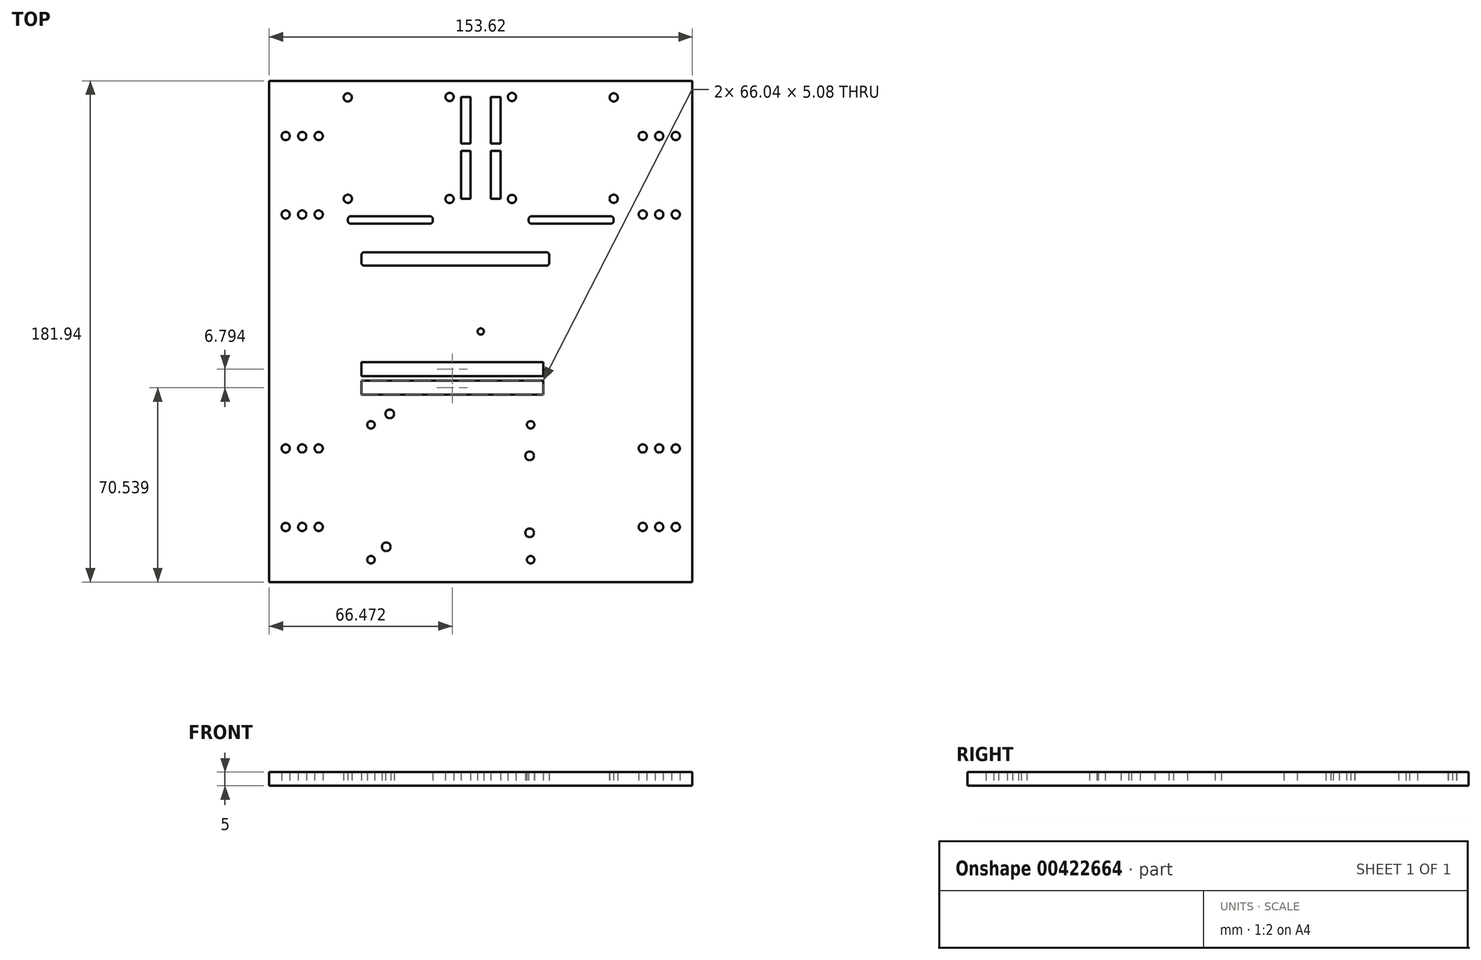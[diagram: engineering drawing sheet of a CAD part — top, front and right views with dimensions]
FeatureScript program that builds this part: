
annotation { "Feature Type Name" : "Feature", "Feature Type Description" : "" }
export const myFeature = defineFeature(function(context is Context, id is Id, definition is map)
    precondition{}
    {
        {
            var Q0;
            Q0=qCreatedBy(makeId("Top.planeOp"),FACE);
            var sketch = newSketch(context, id + "F0", { "sketchPlane" : qUnion([Q0])});
            skLineSegment(sketch, "E0.bottom", {"start": v(-70.46, 90.97) * mm, "end": v(70.46, 90.97) * mm});
            skLineSegment(sketch, "E0.top", {"start": v(-70.46, -90.97) * mm, "end": v(70.46, -90.97) * mm});
            skLineSegment(sketch, "E0.left", {"start": v(-76.8, 84.62) * mm, "end": v(-76.8, -84.62) * mm});
            skLineSegment(sketch, "E0.right", {"start": v(76.8, 84.62) * mm, "end": v(76.8, -84.62) * mm});
            skPoint(sketch, "E0.middle", {"position": v(0, 0) * mm});
            skPoint(sketch, "E1.visualSharp", {"position": v(76.8, 90.97) * mm});
            skPoint(sketch, "E2.visualSharp", {"position": v(-76.8, 90.97) * mm});
            skPoint(sketch, "E3.visualSharp", {"position": v(-76.8, -90.97) * mm});
            skPoint(sketch, "E4.visualSharp", {"position": v(76.8, -90.97) * mm});
            skCircle(sketch, "E5", {"center": v(70.82, 70.98) * mm, "radius": 1.5 * mm});
            skLineSegment(sketch, "E6", {"start": v(70.82, 70.98) * mm, "end": v(58.84, 70.98) * mm, "construction": true});
            skCircle(sketch, "E7", {"center": v(58.84, 70.98) * mm, "radius": 1.5 * mm});
            skCircle(sketch, "E8", {"center": v(64.82, 70.97) * mm, "radius": 1.5 * mm});
            skLineSegment(sketch, "E9", {"start": v(70.82, 70.98) * mm, "end": v(70.82, 48.45) * mm, "construction": true});
            skLineSegment(sketch, "E10", {"start": v(64.82, 70.97) * mm, "end": v(64.82, 48.45) * mm, "construction": true});
            skLineSegment(sketch, "E11", {"start": v(64.82, 48.45) * mm, "end": v(70.82, 48.45) * mm, "construction": true});
            skCircle(sketch, "E12", {"center": v(70.83, 42.48) * mm, "radius": 1.5 * mm});
            skCircle(sketch, "E13", {"center": v(58.85, 42.48) * mm, "radius": 1.5 * mm});
            skCircle(sketch, "E14", {"center": v(64.83, 42.47) * mm, "radius": 1.5 * mm});
            skCircle(sketch, "E15.MirrorC", {"center": v(-58.84, 70.98) * mm, "radius": 1.5 * mm});
            skCircle(sketch, "E16.MirrorC", {"center": v(-64.82, 70.97) * mm, "radius": 1.5 * mm});
            skCircle(sketch, "E17.MirrorC", {"center": v(-70.82, 70.98) * mm, "radius": 1.5 * mm});
            skCircle(sketch, "E18.MirrorC", {"center": v(-70.83, 42.48) * mm, "radius": 1.5 * mm});
            skCircle(sketch, "E19.MirrorC", {"center": v(-64.83, 42.47) * mm, "radius": 1.5 * mm});
            skCircle(sketch, "E20.MirrorC", {"center": v(-58.85, 42.48) * mm, "radius": 1.5 * mm});
            skCircle(sketch, "E21.MirrorC", {"center": v(-58.85, -42.47) * mm, "radius": 1.5 * mm});
            skCircle(sketch, "E22.MirrorC", {"center": v(-64.83, -42.47) * mm, "radius": 1.5 * mm});
            skCircle(sketch, "E23.MirrorC", {"center": v(-70.83, -42.48) * mm, "radius": 1.5 * mm});
            skCircle(sketch, "E24.MirrorC", {"center": v(-70.82, -70.98) * mm, "radius": 1.5 * mm});
            skCircle(sketch, "E25.MirrorC", {"center": v(-64.82, -70.97) * mm, "radius": 1.5 * mm});
            skCircle(sketch, "E26.MirrorC", {"center": v(-58.84, -70.97) * mm, "radius": 1.5 * mm});
            skCircle(sketch, "E27.MirrorC", {"center": v(58.84, -70.97) * mm, "radius": 1.5 * mm});
            skCircle(sketch, "E28.MirrorC", {"center": v(64.82, -70.97) * mm, "radius": 1.5 * mm});
            skCircle(sketch, "E29.MirrorC", {"center": v(70.82, -70.98) * mm, "radius": 1.5 * mm});
            skCircle(sketch, "E30.MirrorC", {"center": v(70.83, -42.48) * mm, "radius": 1.5 * mm});
            skCircle(sketch, "E31.MirrorC", {"center": v(64.83, -42.47) * mm, "radius": 1.5 * mm});
            skCircle(sketch, "E32.MirrorC", {"center": v(58.85, -42.47) * mm, "radius": 1.5 * mm});
            skLineSegment(sketch, "E33.bottom", {"start": v(-48.34, 48.14) * mm, "end": v(-11.32, 48.14) * mm, "construction": true});
            skLineSegment(sketch, "E33.top", {"start": v(-48.34, 85.15) * mm, "end": v(-11.32, 85.15) * mm, "construction": true});
            skLineSegment(sketch, "E33.left", {"start": v(-48.34, 48.14) * mm, "end": v(-48.34, 85.15) * mm, "construction": true});
            skLineSegment(sketch, "E33.right", {"start": v(-11.32, 48.14) * mm, "end": v(-11.32, 85.15) * mm, "construction": true});
            skCircle(sketch, "E34.MirrorC", {"center": v(-48.3, 85) * mm, "radius": 1.5 * mm});
            skCircle(sketch, "E35.MirrorC", {"center": v(-48.26, 48.18) * mm, "radius": 1.5 * mm});
            skCircle(sketch, "E36.MirrorC", {"center": v(-11.32, 85.15) * mm, "radius": 1.5 * mm});
            skCircle(sketch, "E37.MirrorC", {"center": v(-11.32, 48.14) * mm, "radius": 1.5 * mm});
            skCircle(sketch, "E38.MirrorC", {"center": v(48.26, 48.18) * mm, "radius": 1.5 * mm});
            skCircle(sketch, "E39.MirrorC", {"center": v(11.32, 48.14) * mm, "radius": 1.5 * mm});
            skCircle(sketch, "E40.MirrorC", {"center": v(11.32, 85.15) * mm, "radius": 1.5 * mm});
            skCircle(sketch, "E41.MirrorC", {"center": v(48.3, 85) * mm, "radius": 1.5 * mm});
            skLineSegment(sketch, "E42.bottom", {"start": v(-47.15, 41.85) * mm, "end": v(-31.52, 41.85) * mm});
            skLineSegment(sketch, "E42.top", {"start": v(-47.15, 39.11) * mm, "end": v(-31.52, 39.11) * mm});
            skLineSegment(sketch, "E42.left", {"start": v(-48.26, 40.74) * mm, "end": v(-48.26, 40.23) * mm});
            skLineSegment(sketch, "E42.right", {"start": v(-30.4, 40.74) * mm, "end": v(-30.4, 40.23) * mm});
            skLineSegment(sketch, "E43.bottom", {"start": v(-34.14, 41.85) * mm, "end": v(-18.5, 41.85) * mm});
            skLineSegment(sketch, "E43.top", {"start": v(-34.14, 39.11) * mm, "end": v(-18.5, 39.11) * mm});
            skLineSegment(sketch, "E43.left", {"start": v(-35.26, 40.74) * mm, "end": v(-35.26, 40.23) * mm});
            skLineSegment(sketch, "E43.right", {"start": v(-17.4, 40.74) * mm, "end": v(-17.4, 40.23) * mm});
            skPoint(sketch, "E44.visualSharp", {"position": v(-30.4, 41.85) * mm});
            skArc(sketch, "E44.filletArc", {"start": v(-30.4, 40.74) * mm, "mid": v(-30.72, 41.53) * mm, "end": v(-31.52, 41.85) * mm});
            skPoint(sketch, "E45.visualSharp", {"position": v(-30.4, 39.11) * mm});
            skArc(sketch, "E45.filletArc", {"start": v(-31.52, 39.11) * mm, "mid": v(-30.72, 39.44) * mm, "end": v(-30.4, 40.23) * mm});
            skPoint(sketch, "E46.visualSharp", {"position": v(-48.26, 39.11) * mm});
            skArc(sketch, "E46.filletArc", {"start": v(-48.26, 40.23) * mm, "mid": v(-47.94, 39.44) * mm, "end": v(-47.15, 39.11) * mm});
            skPoint(sketch, "E47.visualSharp", {"position": v(-48.26, 41.85) * mm});
            skArc(sketch, "E47.filletArc", {"start": v(-47.15, 41.85) * mm, "mid": v(-47.94, 41.53) * mm, "end": v(-48.26, 40.74) * mm});
            skPoint(sketch, "E48.visualSharp", {"position": v(-35.26, 41.85) * mm});
            skArc(sketch, "E48.filletArc", {"start": v(-34.14, 41.85) * mm, "mid": v(-34.93, 41.53) * mm, "end": v(-35.26, 40.74) * mm});
            skPoint(sketch, "E49.visualSharp", {"position": v(-35.26, 39.11) * mm});
            skArc(sketch, "E49.filletArc", {"start": v(-35.26, 40.23) * mm, "mid": v(-34.93, 39.44) * mm, "end": v(-34.14, 39.11) * mm});
            skPoint(sketch, "E50.visualSharp", {"position": v(-17.4, 39.11) * mm});
            skArc(sketch, "E50.filletArc", {"start": v(-18.5, 39.11) * mm, "mid": v(-17.72, 39.44) * mm, "end": v(-17.4, 40.23) * mm});
            skPoint(sketch, "E51.visualSharp", {"position": v(-17.4, 41.85) * mm});
            skArc(sketch, "E51.filletArc", {"start": v(-17.4, 40.74) * mm, "mid": v(-17.72, 41.53) * mm, "end": v(-18.5, 41.85) * mm});
            skArc(sketch, "E52.MirrorCS", {"start": v(18.5, 39.11) * mm, "mid": v(17.72, 39.44) * mm, "end": v(17.4, 40.23) * mm});
            skArc(sketch, "E53.MirrorCS", {"start": v(17.4, 40.74) * mm, "mid": v(17.72, 41.53) * mm, "end": v(18.5, 41.85) * mm});
            skLineSegment(sketch, "E54.MirrorCS", {"start": v(17.4, 40.74) * mm, "end": v(17.4, 40.23) * mm});
            skLineSegment(sketch, "E55.MirrorCS", {"start": v(34.14, 41.85) * mm, "end": v(18.5, 41.85) * mm});
            skLineSegment(sketch, "E56.MirrorCS", {"start": v(34.14, 39.11) * mm, "end": v(18.5, 39.11) * mm});
            skArc(sketch, "E57.MirrorCS", {"start": v(34.14, 41.85) * mm, "mid": v(34.93, 41.53) * mm, "end": v(35.26, 40.74) * mm});
            skLineSegment(sketch, "E58.MirrorCS", {"start": v(35.26, 40.74) * mm, "end": v(35.26, 40.23) * mm});
            skArc(sketch, "E59.MirrorCS", {"start": v(35.26, 40.23) * mm, "mid": v(34.93, 39.44) * mm, "end": v(34.14, 39.11) * mm});
            skArc(sketch, "E60.MirrorCS", {"start": v(47.15, 41.85) * mm, "mid": v(47.94, 41.53) * mm, "end": v(48.26, 40.74) * mm});
            skLineSegment(sketch, "E61.MirrorCS", {"start": v(48.26, 40.74) * mm, "end": v(48.26, 40.23) * mm});
            skArc(sketch, "E62.MirrorCS", {"start": v(48.26, 40.23) * mm, "mid": v(47.94, 39.44) * mm, "end": v(47.15, 39.11) * mm});
            skLineSegment(sketch, "E63.MirrorCS", {"start": v(47.15, 39.11) * mm, "end": v(31.52, 39.11) * mm});
            skArc(sketch, "E64.MirrorCS", {"start": v(31.52, 39.11) * mm, "mid": v(30.72, 39.44) * mm, "end": v(30.4, 40.23) * mm});
            skLineSegment(sketch, "E65.MirrorCS", {"start": v(47.15, 41.85) * mm, "end": v(31.52, 41.85) * mm});
            skLineSegment(sketch, "E66.MirrorCS", {"start": v(30.4, 40.74) * mm, "end": v(30.4, 40.23) * mm});
            skArc(sketch, "E67.MirrorCS", {"start": v(30.4, 40.74) * mm, "mid": v(30.72, 41.53) * mm, "end": v(31.52, 41.85) * mm});
            skLineSegment(sketch, "E68.bottom", {"start": v(-3.7, 48.14) * mm, "end": v(-7.19, 48.14) * mm});
            skLineSegment(sketch, "E68.top", {"start": v(-3.7, 65.62) * mm, "end": v(-7.19, 65.62) * mm});
            skLineSegment(sketch, "E68.left", {"start": v(-3.7, 48.14) * mm, "end": v(-3.7, 65.62) * mm});
            skLineSegment(sketch, "E68.right", {"start": v(-7.19, 48.14) * mm, "end": v(-7.19, 65.62) * mm});
            skLineSegment(sketch, "E69.bottom", {"start": v(-3.7, 68.24) * mm, "end": v(-7.19, 68.24) * mm});
            skLineSegment(sketch, "E69.top", {"start": v(-3.7, 85.15) * mm, "end": v(-7.19, 85.15) * mm});
            skLineSegment(sketch, "E69.left", {"start": v(-3.7, 68.24) * mm, "end": v(-3.7, 85.15) * mm});
            skLineSegment(sketch, "E69.right", {"start": v(-7.19, 68.24) * mm, "end": v(-7.19, 85.15) * mm});
            skLineSegment(sketch, "E70.MirrorCS", {"start": v(7.19, 48.14) * mm, "end": v(7.19, 65.62) * mm});
            skLineSegment(sketch, "E71.MirrorCS", {"start": v(3.7, 48.14) * mm, "end": v(7.19, 48.14) * mm});
            skLineSegment(sketch, "E72.MirrorCS", {"start": v(3.7, 48.14) * mm, "end": v(3.7, 65.62) * mm});
            skLineSegment(sketch, "E73.MirrorCS", {"start": v(3.7, 65.62) * mm, "end": v(7.19, 65.62) * mm});
            skLineSegment(sketch, "E74.MirrorCS", {"start": v(3.7, 85.15) * mm, "end": v(7.19, 85.15) * mm});
            skLineSegment(sketch, "E75.MirrorCS", {"start": v(3.7, 68.24) * mm, "end": v(7.19, 68.24) * mm});
            skLineSegment(sketch, "E76.MirrorCS", {"start": v(7.19, 68.24) * mm, "end": v(7.19, 85.15) * mm});
            skLineSegment(sketch, "E77.MirrorCS", {"start": v(3.7, 68.24) * mm, "end": v(3.7, 85.15) * mm});
            skLineSegment(sketch, "E78.bottom", {"start": v(-43.36, -25.46) * mm, "end": v(43.36, -25.46) * mm, "construction": true});
            skLineSegment(sketch, "E78.left", {"start": v(-43.36, -25.46) * mm, "end": v(-43.36, -82.88) * mm, "construction": true});
            skLineSegment(sketch, "E78.right", {"start": v(43.36, -25.46) * mm, "end": v(43.36, -82.88) * mm, "construction": true});
            skPoint(sketch, "E78.middle", {"position": v(0, -54.17) * mm});
            skLineSegment(sketch, "E79", {"start": v(-39.87, -33.89) * mm, "end": v(18.12, -33.89) * mm, "construction": true});
            skLineSegment(sketch, "E80", {"start": v(18.12, -33.89) * mm, "end": v(18.12, -82.88) * mm, "construction": true});
            skCircle(sketch, "E81", {"center": v(-39.87, -33.89) * mm, "radius": 1.36 * mm});
            skCircle(sketch, "E82", {"center": v(18.12, -33.89) * mm, "radius": 1.36 * mm});
            skCircle(sketch, "E83", {"center": v(18.12, -82.88) * mm, "radius": 1.36 * mm});
            skCircle(sketch, "E84", {"center": v(-39.87, -82.88) * mm, "radius": 1.36 * mm});
            skLineSegment(sketch, "E85.bottom", {"start": v(-43.36, -22.97) * mm, "end": v(22.68, -22.97) * mm});
            skLineSegment(sketch, "E85.top", {"start": v(-43.36, -17.9) * mm, "end": v(22.68, -17.9) * mm});
            skLineSegment(sketch, "E85.left", {"start": v(-43.36, -22.97) * mm, "end": v(-43.36, -17.9) * mm});
            skLineSegment(sketch, "E85.right", {"start": v(22.68, -22.97) * mm, "end": v(22.68, -17.9) * mm});
            skCircle(sketch, "E86", {"center": v(0, 0) * mm, "radius": 1.13 * mm});
            skLineSegment(sketch, "E87.bottom", {"start": v(-42.24, 23.88) * mm, "end": v(23.8, 23.88) * mm});
            skLineSegment(sketch, "E87.top", {"start": v(-42.24, 28.8) * mm, "end": v(23.8, 28.8) * mm});
            skLineSegment(sketch, "E87.left", {"start": v(-43.36, 25) * mm, "end": v(-43.36, 27.67) * mm});
            skLineSegment(sketch, "E87.right", {"start": v(24.92, 25) * mm, "end": v(24.92, 27.67) * mm});
            skPoint(sketch, "E88.visualSharp", {"position": v(-43.36, 23.88) * mm});
            skArc(sketch, "E88.filletArc", {"start": v(-43.36, 25) * mm, "mid": v(-43.03, 24.2) * mm, "end": v(-42.24, 23.88) * mm});
            skPoint(sketch, "E89.visualSharp", {"position": v(-43.36, 28.8) * mm});
            skArc(sketch, "E89.filletArc", {"start": v(-42.24, 28.8) * mm, "mid": v(-43.03, 28.46) * mm, "end": v(-43.36, 27.67) * mm});
            skPoint(sketch, "E90.visualSharp", {"position": v(24.92, 28.8) * mm});
            skArc(sketch, "E90.filletArc", {"start": v(24.92, 27.67) * mm, "mid": v(24.6, 28.46) * mm, "end": v(23.8, 28.8) * mm});
            skPoint(sketch, "E91.visualSharp", {"position": v(24.92, 23.88) * mm});
            skArc(sketch, "E91.filletArc", {"start": v(23.8, 23.88) * mm, "mid": v(24.6, 24.2) * mm, "end": v(24.92, 25) * mm});
            skLineSegment(sketch, "E92", {"start": v(-76.8, 84.62) * mm, "end": v(-76.8, 90.97) * mm});
            skLineSegment(sketch, "E93", {"start": v(-70.46, 90.97) * mm, "end": v(-76.8, 90.97) * mm});
            skLineSegment(sketch, "E94", {"start": v(70.46, 90.97) * mm, "end": v(76.8, 90.97) * mm});
            skLineSegment(sketch, "E95", {"start": v(76.8, 84.62) * mm, "end": v(76.8, 90.97) * mm});
            skLineSegment(sketch, "E96", {"start": v(76.8, -84.62) * mm, "end": v(76.8, -90.97) * mm});
            skLineSegment(sketch, "E97", {"start": v(70.46, -90.97) * mm, "end": v(76.8, -90.97) * mm});
            skLineSegment(sketch, "E98", {"start": v(-70.46, -90.97) * mm, "end": v(-76.8, -90.97) * mm});
            skLineSegment(sketch, "E99", {"start": v(-76.8, -90.97) * mm, "end": v(-76.8, -84.62) * mm});
            skLineSegment(sketch, "E100.bottom", {"start": v(15.03, 28.8) * mm, "end": v(19.66, 28.8) * mm});
            skCircle(sketch, "E101", {"center": v(-34.3, -78.19) * mm, "radius": 1.59 * mm});
            skCircle(sketch, "E102", {"center": v(-33.04, -29.93) * mm, "radius": 1.59 * mm});
            skCircle(sketch, "E103", {"center": v(17.76, -45.17) * mm, "radius": 1.59 * mm});
            skCircle(sketch, "E104", {"center": v(17.76, -73.1) * mm, "radius": 1.59 * mm});
            skLineSegment(sketch, "E105.bottom", {"start": v(-43.36, -16.18) * mm, "end": v(22.68, -16.18) * mm});
            skLineSegment(sketch, "E105.top", {"start": v(-43.36, -11.1) * mm, "end": v(22.68, -11.1) * mm});
            skLineSegment(sketch, "E105.left", {"start": v(-43.36, -16.18) * mm, "end": v(-43.36, -11.1) * mm});
            skLineSegment(sketch, "E105.right", {"start": v(22.68, -16.18) * mm, "end": v(22.68, -11.1) * mm});
            skSolve(sketch);
        }
        {
            var Q0;
            Q0 = qSketchRegion(id + "F0", true);
            extrude(context, id + "F1", {"entities" : qUnion([Q0]), "depth" : 5 * mm});
        }
    });
